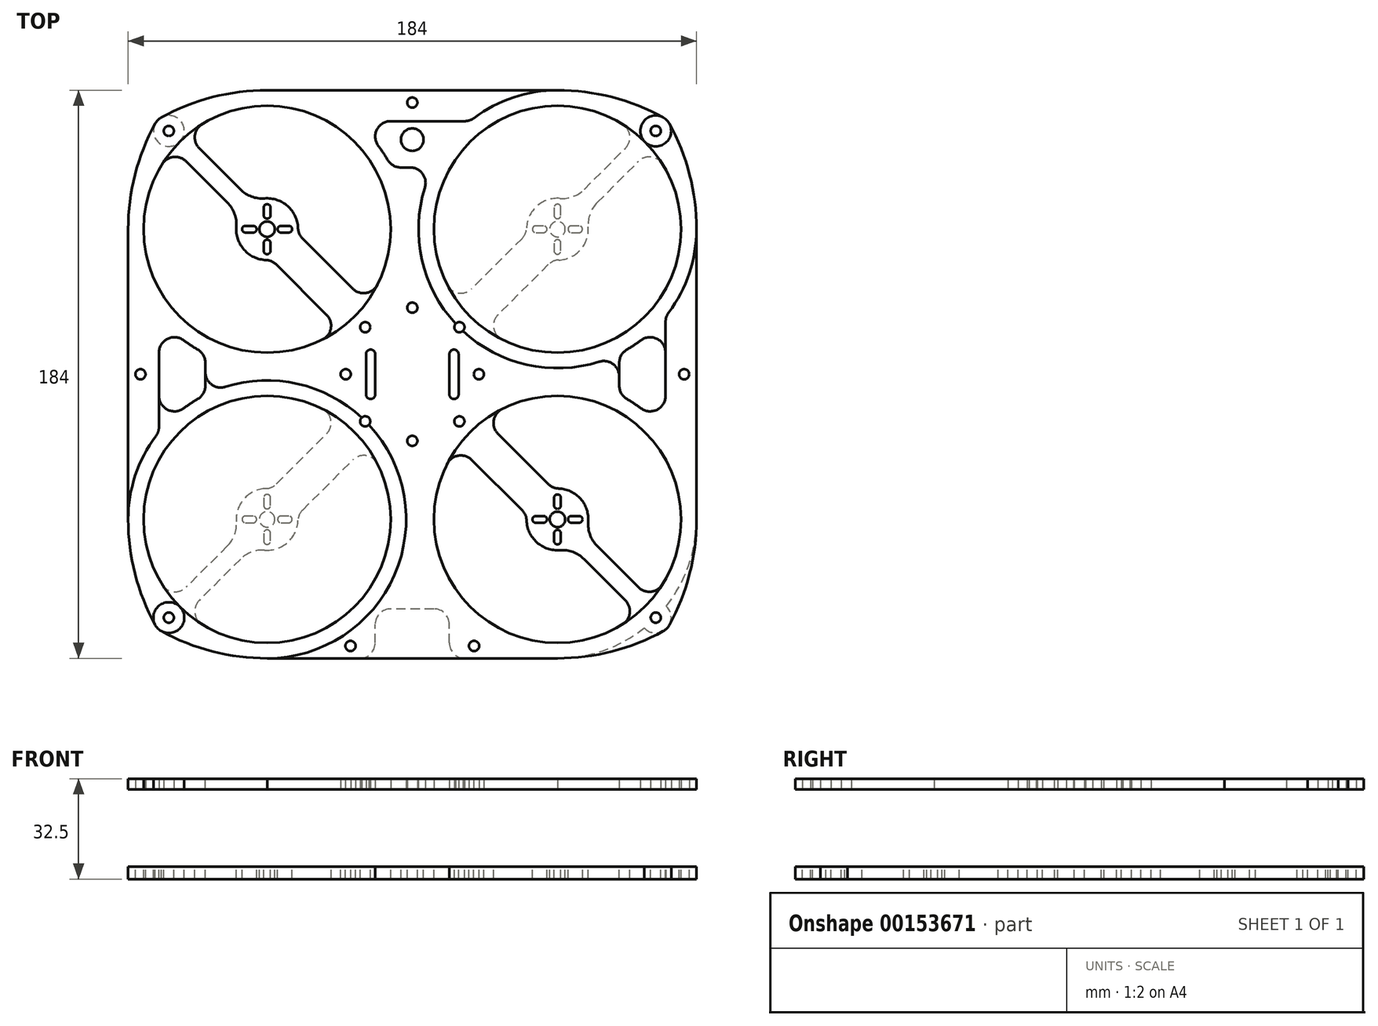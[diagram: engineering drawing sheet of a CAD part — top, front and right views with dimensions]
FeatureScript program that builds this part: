
annotation { "Feature Type Name" : "Feature", "Feature Type Description" : "" }
export const myFeature = defineFeature(function(context is Context, id is Id, definition is map)
    precondition{}
    {
        {
            var Q0;
            Q0=qCreatedBy(makeId("Top.planeOp"),FACE);
            var sketch = newSketch(context, id + "F0", { "sketchPlane" : qUnion([Q0])});
            skCircle(sketch, "E0", {"center": v(-83.32, 39.77) * mm, "radius": 40 * mm});
            skCircle(sketch, "E1", {"center": v(-83.32, 39.77) * mm, "radius": 45 * mm});
            skLineSegment(sketch, "E2", {"start": v(-154.39, -7.23) * mm, "end": v(73.7, -7.23) * mm, "construction": true});
            skLineSegment(sketch, "E3", {"start": v(-36.32, 93.26) * mm, "end": v(-36.32, -114.87) * mm, "construction": true});
            skCircle(sketch, "E4.MirrorC", {"center": v(10.68, 39.77) * mm, "radius": 45 * mm});
            skCircle(sketch, "E5.MirrorC", {"center": v(10.68, 39.77) * mm, "radius": 40 * mm});
            skCircle(sketch, "E6.MirrorC", {"center": v(-83.32, -54.23) * mm, "radius": 40 * mm});
            skCircle(sketch, "E7.MirrorC", {"center": v(-83.32, -54.23) * mm, "radius": 45 * mm});
            skCircle(sketch, "E8.MirrorC", {"center": v(10.68, -54.23) * mm, "radius": 45 * mm});
            skCircle(sketch, "E9.MirrorC", {"center": v(10.68, -54.23) * mm, "radius": 40 * mm});
            skCircle(sketch, "E10", {"center": v(-57.88, -7.23) * mm, "radius": 1.65 * mm});
            skCircle(sketch, "E11", {"center": v(-36.32, 14.33) * mm, "radius": 1.65 * mm});
            skCircle(sketch, "E12", {"center": v(-36.32, -28.8) * mm, "radius": 1.65 * mm});
            skCircle(sketch, "E13", {"center": v(-14.75, -7.23) * mm, "radius": 1.65 * mm});
            skLineSegment(sketch, "E14", {"start": v(-36.32, 14.33) * mm, "end": v(-14.75, -7.23) * mm, "construction": true});
            skLineSegment(sketch, "E15", {"start": v(-57.88, -7.23) * mm, "end": v(-36.32, -28.8) * mm, "construction": true});
            skLineSegment(sketch, "E16", {"start": v(-57.88, -7.23) * mm, "end": v(-36.32, 14.33) * mm, "construction": true});
            skLineSegment(sketch, "E17", {"start": v(-36.32, -28.8) * mm, "end": v(-14.75, -7.23) * mm, "construction": true});
            skLineSegment(sketch, "E18", {"start": v(-36.32, 21.33) * mm, "end": v(-7.75, -7.23) * mm, "construction": true});
            skLineSegment(sketch, "E19", {"start": v(-7.75, -7.23) * mm, "end": v(-36.32, -35.8) * mm, "construction": true});
            skLineSegment(sketch, "E20", {"start": v(-36.32, -35.8) * mm, "end": v(-64.88, -7.23) * mm, "construction": true});
            skLineSegment(sketch, "E21", {"start": v(-64.88, -7.23) * mm, "end": v(-36.32, 21.33) * mm, "construction": true});
            skLineSegment(sketch, "E22", {"start": v(-83.32, 84.77) * mm, "end": v(10.68, 84.77) * mm});
            skLineSegment(sketch, "E23", {"start": v(55.68, 39.77) * mm, "end": v(55.68, -54.23) * mm});
            skLineSegment(sketch, "E24", {"start": v(-83.32, -99.23) * mm, "end": v(10.68, -99.23) * mm});
            skLineSegment(sketch, "E25", {"start": v(-128.32, -54.23) * mm, "end": v(-128.32, 39.77) * mm});
            skLineSegment(sketch, "E26", {"start": v(45.68, -25.95) * mm, "end": v(45.68, 11.48) * mm});
            skLineSegment(sketch, "E27", {"start": v(-118.32, 11.48) * mm, "end": v(-118.32, -25.95) * mm});
            skLineSegment(sketch, "E28", {"start": v(30.68, -0.55) * mm, "end": v(30.68, -13.92) * mm});
            skLineSegment(sketch, "E29", {"start": v(-103.32, -0.55) * mm, "end": v(-103.32, -13.92) * mm});
            skLineSegment(sketch, "E30", {"start": v(-55.03, 74.77) * mm, "end": v(-17.6, 74.77) * mm});
            skLineSegment(sketch, "E31", {"start": v(-43, 59.77) * mm, "end": v(-29.63, 59.77) * mm});
            skCircle(sketch, "E32", {"center": v(-51.57, -22.48) * mm, "radius": 1.65 * mm});
            skCircle(sketch, "E33.MirrorC", {"center": v(-21.07, -22.48) * mm, "radius": 1.65 * mm});
            skCircle(sketch, "E34.MirrorC", {"center": v(-21.07, 8.02) * mm, "radius": 1.65 * mm});
            skCircle(sketch, "E35.MirrorC", {"center": v(-51.57, 8.02) * mm, "radius": 1.65 * mm});
            skCircle(sketch, "E36", {"center": v(-124.32, -7.23) * mm, "radius": 1.65 * mm});
            skCircle(sketch, "E37.MirrorC", {"center": v(51.68, -7.23) * mm, "radius": 1.65 * mm});
            skCircle(sketch, "E38", {"center": v(-36.32, 80.77) * mm, "radius": 1.65 * mm});
            skCircle(sketch, "E39", {"center": v(-56.32, -95.23) * mm, "radius": 1.65 * mm});
            skCircle(sketch, "E40.MirrorC", {"center": v(-16.32, -95.23) * mm, "radius": 1.65 * mm});
            skLineSegment(sketch, "E41.bottom", {"start": v(-51.32, -15.23) * mm, "end": v(-48.32, -15.23) * mm});
            skLineSegment(sketch, "E41.top", {"start": v(-51.32, 0.77) * mm, "end": v(-48.32, 0.77) * mm});
            skLineSegment(sketch, "E41.left", {"start": v(-51.32, -15.23) * mm, "end": v(-51.32, 0.77) * mm});
            skLineSegment(sketch, "E41.right", {"start": v(-48.32, -15.23) * mm, "end": v(-48.32, 0.77) * mm});
            skLineSegment(sketch, "E42.MirrorCS", {"start": v(-66.32, 93.26) * mm, "end": v(-66.32, -114.87) * mm, "construction": true});
            skLineSegment(sketch, "E43.MirrorCS", {"start": v(-24.32, -15.23) * mm, "end": v(-24.32, 0.77) * mm});
            skLineSegment(sketch, "E44.MirrorCS", {"start": v(-21.32, -15.23) * mm, "end": v(-24.32, -15.23) * mm});
            skLineSegment(sketch, "E45.MirrorCS", {"start": v(-21.32, -15.23) * mm, "end": v(-21.32, 0.77) * mm});
            skLineSegment(sketch, "E46.MirrorCS", {"start": v(-21.32, 0.77) * mm, "end": v(-24.32, 0.77) * mm});
            skLineSegment(sketch, "E47", {"start": v(-36.32, -7.23) * mm, "end": v(65.94, 95.02) * mm, "construction": true});
            skLineSegment(sketch, "E48", {"start": v(-36.32, -7.23) * mm, "end": v(-157.97, 114.42) * mm, "construction": true});
            skCircle(sketch, "E49", {"center": v(-115.14, 71.59) * mm, "radius": 1.65 * mm});
            skCircle(sketch, "E50", {"center": v(-115.14, 71.59) * mm, "radius": 5 * mm});
            skArc(sketch, "E51", {"start": v(-83.32, 84.77) * mm, "mid": v(-100.99, 82.53) * mm, "end": v(-117.55, 75.97) * mm});
            skArc(sketch, "E52", {"start": v(-119.52, 74) * mm, "mid": v(-126.08, 57.44) * mm, "end": v(-128.32, 39.77) * mm});
            skArc(sketch, "E53.MirrorCS", {"start": v(10.68, 84.77) * mm, "mid": v(28.36, 82.53) * mm, "end": v(44.92, 75.97) * mm});
            skArc(sketch, "E54.MirrorCS", {"start": v(46.88, 74) * mm, "mid": v(53.45, 57.44) * mm, "end": v(55.68, 39.77) * mm});
            skCircle(sketch, "E55.MirrorC", {"center": v(42.5, 71.59) * mm, "radius": 1.65 * mm});
            skCircle(sketch, "E56.MirrorC", {"center": v(42.5, 71.59) * mm, "radius": 5 * mm});
            skArc(sketch, "E57.MirrorCS", {"start": v(46.88, -88.47) * mm, "mid": v(53.45, -71.9) * mm, "end": v(55.68, -54.23) * mm});
            skCircle(sketch, "E58.MirrorC", {"center": v(42.5, -86.05) * mm, "radius": 5 * mm});
            skCircle(sketch, "E59.MirrorC", {"center": v(42.5, -86.05) * mm, "radius": 1.65 * mm});
            skArc(sketch, "E60.MirrorCS", {"start": v(10.68, -99.23) * mm, "mid": v(28.36, -97) * mm, "end": v(44.92, -90.43) * mm});
            skArc(sketch, "E61.MirrorCS", {"start": v(-83.32, -99.23) * mm, "mid": v(-100.99, -97) * mm, "end": v(-117.55, -90.43) * mm});
            skCircle(sketch, "E62.MirrorC", {"center": v(-115.14, -86.05) * mm, "radius": 5 * mm});
            skCircle(sketch, "E63.MirrorC", {"center": v(-115.14, -86.05) * mm, "radius": 1.65 * mm});
            skArc(sketch, "E64.MirrorCS", {"start": v(-119.52, -88.47) * mm, "mid": v(-126.08, -71.9) * mm, "end": v(-128.32, -54.23) * mm});
            skSolve(sketch);
        }
        {
            var Q0;
            {var subQ0=sQuery(id+"F0.wireOp",EDGE,"E25");Q0=makeQuery(id+"F0.imprint","IMPRINT",FACE,{"disambiguationData":[TD([[makeQuery(id+"F0.imprint","IMPRINT",EDGE,{"derivedFrom":subQ0}),-1.0]])]});}
            var Q1;
            Q1=makeQuery(id+"F0.imprint","IMPRINT",FACE,{"disambiguationData":[TD([[makeQuery(id+"F0.imprint","IMPRINT",EDGE,{"derivedFrom":sQuery(id+"F0.wireOp",EDGE,"E0")}),-1.0]])]});
            var Q2;
            Q2=makeQuery(id+"F0.imprint","IMPRINT",FACE,{"disambiguationData":[TD([[makeQuery(id+"F0.imprint","IMPRINT",EDGE,{"derivedFrom":sQuery(id+"F0.wireOp",EDGE,"E10")}),-1.0]])]});
            var Q3;
            Q3=makeQuery(id+"F0.imprint","IMPRINT",FACE,{"disambiguationData":[TD([[makeQuery(id+"F0.imprint","IMPRINT",EDGE,{"derivedFrom":sQuery(id+"F0.wireOp",EDGE,"E5.MirrorC")}),1.0]])]});
            var Q4;
            {var subQ0=sQuery(id+"F0.wireOp",EDGE,"E23");Q4=makeQuery(id+"F0.imprint","IMPRINT",FACE,{"disambiguationData":[TD([[makeQuery(id+"F0.imprint","IMPRINT",EDGE,{"derivedFrom":subQ0}),-1.0]])]});}
            var Q5;
            Q5=makeQuery(id+"F0.imprint","IMPRINT",FACE,{"disambiguationData":[TD([[makeQuery(id+"F0.imprint","IMPRINT",EDGE,{"derivedFrom":sQuery(id+"F0.wireOp",EDGE,"E6.MirrorC")}),1.0]])]});
            var Q6;
            Q6=makeQuery(id+"F0.imprint","IMPRINT",FACE,{"disambiguationData":[TD([[makeQuery(id+"F0.imprint","IMPRINT",EDGE,{"derivedFrom":sQuery(id+"F0.wireOp",EDGE,"E9.MirrorC")}),-1.0]])]});
            var Q7;
            {var subQ0=sQuery(id+"F0.wireOp",EDGE,"E22");Q7=makeQuery(id+"F0.imprint","IMPRINT",FACE,{"disambiguationData":[TD([[makeQuery(id+"F0.imprint","IMPRINT",EDGE,{"derivedFrom":subQ0}),-1.0]])]});}
            var Q8;
            {var subQ0=sQuery(id+"F0.wireOp",EDGE,"E50");var subQ2=sQuery(id+"F0.wireOp",EDGE,"E1");var subQ4=makeQuery(id+"F0.imprint","INTERSECT",VERTEX,{"disambiguationData":[OD(0.0)],"derivedFrom":[subQ2,subQ0]});Q8=makeQuery(id+"F0.imprint","IMPRINT",FACE,{"disambiguationData":[TD([[makeQuery(id+"F0.imprint","IMPRINT",EDGE,{"disambiguationData":[TD([[subQ4,-1.0]])],"derivedFrom":subQ2}),1.0]])]});}
            var Q9;
            {var subQ0=sQuery(id+"F0.wireOp",EDGE,"E51");Q9=makeQuery(id+"F0.imprint","IMPRINT",FACE,{"disambiguationData":[TD([[makeQuery(id+"F0.imprint","IMPRINT",EDGE,{"derivedFrom":subQ0}),1.0]])]});}
            var Q10;
            {var subQ0=sQuery(id+"F0.wireOp",EDGE,"E50");var subQ2=sQuery(id+"F0.wireOp",EDGE,"E1");var subQ3=makeQuery(id+"F0.imprint","INTERSECT",VERTEX,{"disambiguationData":[OD(0.0)],"derivedFrom":[subQ2,subQ0]});Q10=makeQuery(id+"F0.imprint","IMPRINT",FACE,{"disambiguationData":[TD([[makeQuery(id+"F0.imprint","IMPRINT",EDGE,{"disambiguationData":[TD([[subQ3,-1.0]])],"derivedFrom":subQ2}),-1.0]])]});}
            var Q11;
            {var subQ0=sQuery(id+"F0.wireOp",EDGE,"E52");Q11=makeQuery(id+"F0.imprint","IMPRINT",FACE,{"disambiguationData":[TD([[makeQuery(id+"F0.imprint","IMPRINT",EDGE,{"derivedFrom":subQ0}),1.0]])]});}
            var Q12;
            {var subQ0=sQuery(id+"F0.wireOp",EDGE,"E54.MirrorCS");Q12=makeQuery(id+"F0.imprint","IMPRINT",FACE,{"disambiguationData":[TD([[makeQuery(id+"F0.imprint","IMPRINT",EDGE,{"derivedFrom":subQ0}),-1.0]])]});}
            var Q13;
            {var subQ1=sQuery(id+"F0.wireOp",EDGE,"E4.MirrorC");var subQ4=sQuery(id+"F0.wireOp",EDGE,"E56.MirrorC");var subQ6=makeQuery(id+"F0.imprint","INTERSECT",VERTEX,{"disambiguationData":[OD(0.0)],"derivedFrom":[subQ1,subQ4]});Q13=makeQuery(id+"F0.imprint","IMPRINT",FACE,{"disambiguationData":[TD([[makeQuery(id+"F0.imprint","IMPRINT",EDGE,{"disambiguationData":[TD([[subQ6,-1.0]])],"derivedFrom":subQ1}),1.0]])]});}
            var Q14;
            {var subQ0=sQuery(id+"F0.wireOp",EDGE,"E53.MirrorCS");Q14=makeQuery(id+"F0.imprint","IMPRINT",FACE,{"disambiguationData":[TD([[makeQuery(id+"F0.imprint","IMPRINT",EDGE,{"derivedFrom":subQ0}),-1.0]])]});}
            var Q15;
            {var subQ1=sQuery(id+"F0.wireOp",EDGE,"E4.MirrorC");var subQ4=sQuery(id+"F0.wireOp",EDGE,"E56.MirrorC");var subQ7=makeQuery(id+"F0.imprint","INTERSECT",VERTEX,{"disambiguationData":[OD(0.0)],"derivedFrom":[subQ1,subQ4]});Q15=makeQuery(id+"F0.imprint","IMPRINT",FACE,{"disambiguationData":[TD([[makeQuery(id+"F0.imprint","IMPRINT",EDGE,{"disambiguationData":[TD([[subQ7,-1.0]])],"derivedFrom":subQ1}),-1.0]])]});}
            var Q16;
            {var subQ0=sQuery(id+"F0.wireOp",EDGE,"E28");Q16=makeQuery(id+"F0.imprint","IMPRINT",FACE,{"disambiguationData":[TD([[makeQuery(id+"F0.imprint","IMPRINT",EDGE,{"derivedFrom":subQ0}),-1.0]])]});}
            var Q17;
            {var subQ0=sQuery(id+"F0.wireOp",EDGE,"E29");Q17=makeQuery(id+"F0.imprint","IMPRINT",FACE,{"disambiguationData":[TD([[makeQuery(id+"F0.imprint","IMPRINT",EDGE,{"derivedFrom":subQ0}),1.0]])]});}
            var Q18;
            {var subQ0=sQuery(id+"F0.wireOp",EDGE,"E58.MirrorC");var subQ4=sQuery(id+"F0.wireOp",EDGE,"E8.MirrorC");var subQ7=makeQuery(id+"F0.imprint","INTERSECT",VERTEX,{"disambiguationData":[OD(0.0)],"derivedFrom":[subQ4,subQ0]});Q18=makeQuery(id+"F0.imprint","IMPRINT",FACE,{"disambiguationData":[TD([[makeQuery(id+"F0.imprint","IMPRINT",EDGE,{"disambiguationData":[TD([[subQ7,-1.0]])],"derivedFrom":subQ4}),-1.0]])]});}
            var Q19;
            {var subQ0=sQuery(id+"F0.wireOp",EDGE,"E57.MirrorCS");Q19=makeQuery(id+"F0.imprint","IMPRINT",FACE,{"disambiguationData":[TD([[makeQuery(id+"F0.imprint","IMPRINT",EDGE,{"derivedFrom":subQ0}),1.0]])]});}
            var Q20;
            {var subQ0=sQuery(id+"F0.wireOp",EDGE,"E58.MirrorC");var subQ2=sQuery(id+"F0.wireOp",EDGE,"E8.MirrorC");var subQ3=makeQuery(id+"F0.imprint","INTERSECT",VERTEX,{"disambiguationData":[OD(0.0)],"derivedFrom":[subQ2,subQ0]});Q20=makeQuery(id+"F0.imprint","IMPRINT",FACE,{"disambiguationData":[TD([[makeQuery(id+"F0.imprint","IMPRINT",EDGE,{"disambiguationData":[TD([[subQ3,-1.0]])],"derivedFrom":subQ2}),1.0]])]});}
            var Q21;
            {var subQ0=sQuery(id+"F0.wireOp",EDGE,"E60.MirrorCS");Q21=makeQuery(id+"F0.imprint","IMPRINT",FACE,{"disambiguationData":[TD([[makeQuery(id+"F0.imprint","IMPRINT",EDGE,{"derivedFrom":subQ0}),1.0]])]});}
            var Q22;
            {var subQ0=sQuery(id+"F0.wireOp",EDGE,"E61.MirrorCS");Q22=makeQuery(id+"F0.imprint","IMPRINT",FACE,{"disambiguationData":[TD([[makeQuery(id+"F0.imprint","IMPRINT",EDGE,{"derivedFrom":subQ0}),-1.0]])]});}
            var Q23;
            {var subQ0=sQuery(id+"F0.wireOp",EDGE,"E62.MirrorC");var subQ2=sQuery(id+"F0.wireOp",EDGE,"E7.MirrorC");var subQ3=makeQuery(id+"F0.imprint","INTERSECT",VERTEX,{"disambiguationData":[OD(0.0)],"derivedFrom":[subQ2,subQ0]});Q23=makeQuery(id+"F0.imprint","IMPRINT",FACE,{"disambiguationData":[TD([[makeQuery(id+"F0.imprint","IMPRINT",EDGE,{"disambiguationData":[TD([[subQ3,-1.0]])],"derivedFrom":subQ2}),1.0]])]});}
            var Q24;
            {var subQ1=sQuery(id+"F0.wireOp",EDGE,"E7.MirrorC");var subQ3=sQuery(id+"F0.wireOp",EDGE,"E62.MirrorC");var subQ6=makeQuery(id+"F0.imprint","INTERSECT",VERTEX,{"disambiguationData":[OD(0.0)],"derivedFrom":[subQ1,subQ3]});Q24=makeQuery(id+"F0.imprint","IMPRINT",FACE,{"disambiguationData":[TD([[makeQuery(id+"F0.imprint","IMPRINT",EDGE,{"disambiguationData":[TD([[subQ6,-1.0]])],"derivedFrom":subQ1}),-1.0]])]});}
            var Q25;
            {var subQ0=sQuery(id+"F0.wireOp",EDGE,"E64.MirrorCS");Q25=makeQuery(id+"F0.imprint","IMPRINT",FACE,{"disambiguationData":[TD([[makeQuery(id+"F0.imprint","IMPRINT",EDGE,{"derivedFrom":subQ0}),-1.0]])]});}
            extrude(context, id + "F1", {"entities" : qUnion([Q0, Q1, Q2, Q3, Q4, Q5, Q6, Q7, Q8, Q9, Q10, Q11, Q12, Q13, Q14, Q15, Q16, Q17, Q18, Q19, Q20, Q21, Q22, Q23, Q24, Q25]), "depth" : 3.5 * mm});
        }
        {
            var Q0;
            Q0=makeQuery(id+"F1.opExtrude","SWEPT_EDGE",EDGE,{"disambiguationData":[OSD([sQuery(id+"F0.wireOp",EDGE,"E1"),sQuery(id+"F0.wireOp",EDGE,"E27")])]});
            var Q1;
            Q1=makeQuery(id+"F1.opExtrude","SWEPT_EDGE",EDGE,{"disambiguationData":[OSD([sQuery(id+"F0.wireOp",EDGE,"E4.MirrorC"),sQuery(id+"F0.wireOp",EDGE,"E26")])]});
            var Q2;
            Q2=makeQuery(id+"F1.opExtrude","SWEPT_EDGE",EDGE,{"disambiguationData":[OSD([sQuery(id+"F0.wireOp",EDGE,"E8.MirrorC"),sQuery(id+"F0.wireOp",EDGE,"E26")])]});
            var Q3;
            Q3=makeQuery(id+"F1.opExtrude","SWEPT_EDGE",EDGE,{"disambiguationData":[OSD([sQuery(id+"F0.wireOp",EDGE,"E7.MirrorC"),sQuery(id+"F0.wireOp",EDGE,"E27")])]});
            var Q4;
            Q4=makeQuery(id+"F1.opExtrude","SWEPT_EDGE",EDGE,{"disambiguationData":[OSD([sQuery(id+"F0.wireOp",EDGE,"E4.MirrorC"),sQuery(id+"F0.wireOp",EDGE,"E30")])]});
            var Q5;
            Q5=makeQuery(id+"F1.opExtrude","SWEPT_EDGE",EDGE,{"disambiguationData":[OSD([sQuery(id+"F0.wireOp",EDGE,"E1"),sQuery(id+"F0.wireOp",EDGE,"E30")])]});
            fillet(context, id + "F2", {"entities" : qUnion([Q0, Q1, Q2, Q3, Q4, Q5]), "radius" : 5 * mm, "tangentPropagation" : true, "allowEdgeOverflow" : false});
        }
        {
            var Q0;
            Q0=makeQuery(id+"F1.opExtrude","SWEPT_EDGE",EDGE,{"disambiguationData":[OSD([sQuery(id+"F0.wireOp",EDGE,"E4.MirrorC"),sQuery(id+"F0.wireOp",EDGE,"E28")])]});
            var Q1;
            Q1=makeQuery(id+"F1.opExtrude","SWEPT_EDGE",EDGE,{"disambiguationData":[OSD([sQuery(id+"F0.wireOp",EDGE,"E8.MirrorC"),sQuery(id+"F0.wireOp",EDGE,"E28")])]});
            var Q2;
            Q2=makeQuery(id+"F1.opExtrude","SWEPT_EDGE",EDGE,{"disambiguationData":[OSD([sQuery(id+"F0.wireOp",EDGE,"E1"),sQuery(id+"F0.wireOp",EDGE,"E29")])]});
            var Q3;
            Q3=makeQuery(id+"F1.opExtrude","SWEPT_EDGE",EDGE,{"disambiguationData":[OSD([sQuery(id+"F0.wireOp",EDGE,"E7.MirrorC"),sQuery(id+"F0.wireOp",EDGE,"E29")])]});
            var Q4;
            Q4=makeQuery(id+"F1.opExtrude","SWEPT_EDGE",EDGE,{"disambiguationData":[OSD([sQuery(id+"F0.wireOp",EDGE,"E4.MirrorC"),sQuery(id+"F0.wireOp",EDGE,"E31")])]});
            var Q5;
            Q5=makeQuery(id+"F1.opExtrude","SWEPT_EDGE",EDGE,{"disambiguationData":[OSD([sQuery(id+"F0.wireOp",EDGE,"E1"),sQuery(id+"F0.wireOp",EDGE,"E31")])]});
            fillet(context, id + "F3", {"entities" : qUnion([Q0, Q1, Q2, Q3, Q4, Q5]), "radius" : 5 * mm, "tangentPropagation" : true, "allowEdgeOverflow" : false});
        }
        {
            var Q0;
            Q0=makeQuery(id+"F1.opExtrude","SWEPT_EDGE",EDGE,{"disambiguationData":[OSD([sQuery(id+"F0.wireOp",EDGE,"E41.bottom"),sQuery(id+"F0.wireOp",EDGE,"E41.left")])]});
            var Q1;
            Q1=makeQuery(id+"F1.opExtrude","SWEPT_EDGE",EDGE,{"disambiguationData":[OSD([sQuery(id+"F0.wireOp",EDGE,"E43.MirrorCS"),sQuery(id+"F0.wireOp",EDGE,"E44.MirrorCS")])]});
            var Q2;
            Q2=makeQuery(id+"F1.opExtrude","SWEPT_EDGE",EDGE,{"disambiguationData":[OSD([sQuery(id+"F0.wireOp",EDGE,"E41.bottom"),sQuery(id+"F0.wireOp",EDGE,"E41.right")])]});
            var Q3;
            Q3=makeQuery(id+"F1.opExtrude","SWEPT_EDGE",EDGE,{"disambiguationData":[OSD([sQuery(id+"F0.wireOp",EDGE,"E44.MirrorCS"),sQuery(id+"F0.wireOp",EDGE,"E45.MirrorCS")])]});
            var Q4;
            Q4=makeQuery(id+"F1.opExtrude","SWEPT_EDGE",EDGE,{"disambiguationData":[OSD([sQuery(id+"F0.wireOp",EDGE,"E43.MirrorCS"),sQuery(id+"F0.wireOp",EDGE,"E46.MirrorCS")])]});
            var Q5;
            Q5=makeQuery(id+"F1.opExtrude","SWEPT_EDGE",EDGE,{"disambiguationData":[OSD([sQuery(id+"F0.wireOp",EDGE,"E41.top"),sQuery(id+"F0.wireOp",EDGE,"E41.left")])]});
            var Q6;
            Q6=makeQuery(id+"F1.opExtrude","SWEPT_EDGE",EDGE,{"disambiguationData":[OSD([sQuery(id+"F0.wireOp",EDGE,"E45.MirrorCS"),sQuery(id+"F0.wireOp",EDGE,"E46.MirrorCS")])]});
            var Q7;
            Q7=makeQuery(id+"F1.opExtrude","SWEPT_EDGE",EDGE,{"disambiguationData":[OSD([sQuery(id+"F0.wireOp",EDGE,"E41.top"),sQuery(id+"F0.wireOp",EDGE,"E41.right")])]});
            fillet(context, id + "F4", {"entities" : qUnion([Q0, Q1, Q2, Q3, Q4, Q5, Q6, Q7]), "radius" : 1.5 * mm, "tangentPropagation" : true, "allowEdgeOverflow" : false});
        }
        {
            var Q0;
            Q0=makeQuery(id+"F1.opExtrude","CAP_FACE",FACE,{"disambiguationData":[OSD([sQuery(id+"F0.wireOp",EDGE,"E0"),sQuery(id+"F0.wireOp",EDGE,"E1"),sQuery(id+"F0.wireOp",EDGE,"E4.MirrorC"),sQuery(id+"F0.wireOp",EDGE,"E5.MirrorC"),sQuery(id+"F0.wireOp",EDGE,"E6.MirrorC"),sQuery(id+"F0.wireOp",EDGE,"E7.MirrorC"),sQuery(id+"F0.wireOp",EDGE,"E8.MirrorC"),sQuery(id+"F0.wireOp",EDGE,"E9.MirrorC"),sQuery(id+"F0.wireOp",EDGE,"E10"),sQuery(id+"F0.wireOp",EDGE,"E11"),sQuery(id+"F0.wireOp",EDGE,"E12"),sQuery(id+"F0.wireOp",EDGE,"E13"),sQuery(id+"F0.wireOp",EDGE,"E22"),sQuery(id+"F0.wireOp",EDGE,"E23"),sQuery(id+"F0.wireOp",EDGE,"E24"),sQuery(id+"F0.wireOp",EDGE,"E25"),sQuery(id+"F0.wireOp",EDGE,"E26"),sQuery(id+"F0.wireOp",EDGE,"E27"),sQuery(id+"F0.wireOp",EDGE,"E28"),sQuery(id+"F0.wireOp",EDGE,"E29"),sQuery(id+"F0.wireOp",EDGE,"E30"),sQuery(id+"F0.wireOp",EDGE,"E31"),sQuery(id+"F0.wireOp",EDGE,"E32"),sQuery(id+"F0.wireOp",EDGE,"E33.MirrorC"),sQuery(id+"F0.wireOp",EDGE,"E34.MirrorC"),sQuery(id+"F0.wireOp",EDGE,"E35.MirrorC"),sQuery(id+"F0.wireOp",EDGE,"E36"),sQuery(id+"F0.wireOp",EDGE,"E37.MirrorC"),sQuery(id+"F0.wireOp",EDGE,"E38"),sQuery(id+"F0.wireOp",EDGE,"E39"),sQuery(id+"F0.wireOp",EDGE,"E40.MirrorC"),sQuery(id+"F0.wireOp",EDGE,"E41.bottom"),sQuery(id+"F0.wireOp",EDGE,"E41.top"),sQuery(id+"F0.wireOp",EDGE,"E41.left"),sQuery(id+"F0.wireOp",EDGE,"E41.right"),sQuery(id+"F0.wireOp",EDGE,"E43.MirrorCS"),sQuery(id+"F0.wireOp",EDGE,"E44.MirrorCS"),sQuery(id+"F0.wireOp",EDGE,"E45.MirrorCS"),sQuery(id+"F0.wireOp",EDGE,"E46.MirrorCS")])],"isStart":true});
            cPlane(context, id + "F5", {"entities" : qUnion([Q0]), "cplaneType" : CPlaneType.OFFSET, "offset" : 25 * mm, "width" : 150 * mm, "height" : 150 * mm});
        }
        {
            var Q0;
            Q0=qCreatedBy(id+"F5.planeOp",FACE);
            var sketch = newSketch(context, id + "F6", { "sketchPlane" : qUnion([Q0])});
            skLineSegment(sketch, "E65.0", {"start": v(-110.32, 18.23) * mm, "end": v(-110.32, 18.23) * mm});
            skLineSegment(sketch, "E66.0", {"start": v(-128.32, 57.23) * mm, "end": v(-128.32, -39.77) * mm});
            skLineSegment(sketch, "E67.0", {"start": v(-83.32, -84.77) * mm, "end": v(10.68, -84.77) * mm});
            skLineSegment(sketch, "E68.0", {"start": v(55.68, -39.77) * mm, "end": v(55.68, 54.23) * mm});
            skLineSegment(sketch, "E69.0", {"start": v(-86.32, 99.23) * mm, "end": v(10.68, 99.23) * mm});
            skArc(sketch, "E70.0", {"start": v(10.68, 99.23) * mm, "mid": v(42.5, 86.05) * mm, "end": v(55.68, 54.23) * mm});
            skCircle(sketch, "E71.0", {"center": v(51.68, 7.23) * mm, "radius": 1.65 * mm});
            skCircle(sketch, "E72.0", {"center": v(-16.32, 95.23) * mm, "radius": 1.65 * mm});
            skCircle(sketch, "E73.0", {"center": v(-56.32, 95.23) * mm, "radius": 1.65 * mm});
            skCircle(sketch, "E74.0", {"center": v(-124.32, 7.23) * mm, "radius": 1.65 * mm});
            skCircle(sketch, "E75.0", {"center": v(-36.32, -80.77) * mm, "radius": 1.65 * mm});
            skCircle(sketch, "E76.0", {"center": v(10.68, -39.77) * mm, "radius": 40 * mm});
            skCircle(sketch, "E77.0", {"center": v(-83.32, -39.77) * mm, "radius": 40 * mm});
            skCircle(sketch, "E78.0", {"center": v(-83.32, 54.23) * mm, "radius": 40 * mm});
            skCircle(sketch, "E79.0", {"center": v(10.68, 54.23) * mm, "radius": 40 * mm});
            skLineSegment(sketch, "E80.0", {"start": v(-21.32, 13.73) * mm, "end": v(-21.32, 0.73) * mm});
            skLineSegment(sketch, "E81.0", {"start": v(-24.32, 13.73) * mm, "end": v(-24.32, 0.73) * mm});
            skLineSegment(sketch, "E82.0", {"start": v(-48.32, 13.73) * mm, "end": v(-48.32, 0.73) * mm});
            skLineSegment(sketch, "E83.0", {"start": v(-51.32, 13.73) * mm, "end": v(-51.32, 0.73) * mm});
            skCircle(sketch, "E84.0", {"center": v(-51.57, 22.48) * mm, "radius": 1.65 * mm});
            skCircle(sketch, "E85.0", {"center": v(-36.32, 28.8) * mm, "radius": 1.65 * mm});
            skCircle(sketch, "E86.0", {"center": v(-14.75, 7.23) * mm, "radius": 1.65 * mm});
            skCircle(sketch, "E87.0", {"center": v(-36.32, -14.33) * mm, "radius": 1.65 * mm});
            skCircle(sketch, "E88.0", {"center": v(-51.57, -8.02) * mm, "radius": 1.65 * mm});
            skCircle(sketch, "E89.0", {"center": v(-57.88, 7.23) * mm, "radius": 1.65 * mm});
            skCircle(sketch, "E90.0", {"center": v(-21.07, -8.02) * mm, "radius": 1.65 * mm});
            skCircle(sketch, "E91.0", {"center": v(-21.07, 22.48) * mm, "radius": 1.65 * mm});
            skLineSegment(sketch, "E92.0", {"start": v(45.68, 14.23) * mm, "end": v(45.68, 0.23) * mm});
            skArc(sketch, "E92.1", {"start": v(45.68, 0.23) * mm, "mid": v(42.92, -4.24) * mm, "end": v(37.68, -3.77) * mm});
            skLineSegment(sketch, "E92.2", {"start": v(30.68, 3.54) * mm, "end": v(30.68, 10.93) * mm});
            skArc(sketch, "E92.3", {"start": v(37.68, 18.23) * mm, "mid": v(35.48, 16.68) * mm, "end": v(33.18, 15.26) * mm});
            skArc(sketch, "E92.4", {"start": v(37.68, 18.23) * mm, "mid": v(42.92, 18.7) * mm, "end": v(45.68, 14.23) * mm});
            skPoint(sketch, "E92.5", {"position": v(33.18, 15.26) * mm});
            skArc(sketch, "E93.0", {"start": v(30.68, 10.93) * mm, "mid": v(31.35, 13.43) * mm, "end": v(33.18, 15.26) * mm});
            skArc(sketch, "E94.0", {"start": v(33.18, -0.8) * mm, "mid": v(31.35, 1.04) * mm, "end": v(30.68, 3.54) * mm});
            skArc(sketch, "E94.1", {"start": v(37.68, -3.77) * mm, "mid": v(35.48, -2.21) * mm, "end": v(33.18, -0.8) * mm});
            skArc(sketch, "E95.0", {"start": v(-21.32, 0.73) * mm, "mid": v(-22.82, -0.77) * mm, "end": v(-24.32, 0.73) * mm});
            skArc(sketch, "E96.0", {"start": v(-24.32, 13.73) * mm, "mid": v(-22.82, 15.23) * mm, "end": v(-21.32, 13.73) * mm});
            skArc(sketch, "E97.0", {"start": v(-51.32, 13.73) * mm, "mid": v(-49.82, 15.23) * mm, "end": v(-48.32, 13.73) * mm});
            skArc(sketch, "E98.0", {"start": v(-48.32, 0.73) * mm, "mid": v(-49.82, -0.77) * mm, "end": v(-51.32, 0.73) * mm});
            skArc(sketch, "E99.0", {"start": v(-110.32, -3.77) * mm, "mid": v(-108.11, -2.21) * mm, "end": v(-105.82, -0.8) * mm});
            skArc(sketch, "E99.1", {"start": v(-103.32, 3.54) * mm, "mid": v(-103.99, 1.04) * mm, "end": v(-105.82, -0.8) * mm});
            skLineSegment(sketch, "E99.2", {"start": v(-103.32, 3.54) * mm, "end": v(-103.32, 10.93) * mm});
            skArc(sketch, "E99.3", {"start": v(-105.82, 15.26) * mm, "mid": v(-103.99, 13.43) * mm, "end": v(-103.32, 10.93) * mm});
            skArc(sketch, "E99.4", {"start": v(-110.32, 18.23) * mm, "mid": v(-108.11, 16.68) * mm, "end": v(-105.82, 15.26) * mm});
            skArc(sketch, "E99.5", {"start": v(-118.32, 14.23) * mm, "mid": v(-115.55, 18.7) * mm, "end": v(-110.32, 18.23) * mm});
            skLineSegment(sketch, "E99.6", {"start": v(-118.32, 0.23) * mm, "end": v(-118.32, 14.23) * mm});
            skArc(sketch, "E99.7", {"start": v(-110.32, -3.77) * mm, "mid": v(-115.55, -4.24) * mm, "end": v(-118.32, 0.23) * mm});
            skCircle(sketch, "E100", {"center": v(-83.32, 54.23) * mm, "radius": 10 * mm});
            skLineSegment(sketch, "E101.0", {"start": v(-36.32, -93.26) * mm, "end": v(-36.32, 114.87) * mm, "construction": true});
            skLineSegment(sketch, "E102.0", {"start": v(-154.39, 7.23) * mm, "end": v(73.7, 7.23) * mm, "construction": true});
            skLineSegment(sketch, "E103", {"start": v(-36.32, 7.23) * mm, "end": v(-115.14, 86.05) * mm, "construction": true});
            skLineSegment(sketch, "E104", {"start": v(-92.18, 58.86) * mm, "end": v(-113.64, 80.32) * mm});
            skLineSegment(sketch, "E105", {"start": v(-87.94, 63.1) * mm, "end": v(-109.4, 84.56) * mm});
            skCircle(sketch, "E106", {"center": v(-83.32, 54.23) * mm, "radius": 2.5 * mm});
            skLineSegment(sketch, "E107", {"start": v(-83.32, 64.23) * mm, "end": v(-83.32, 44.23) * mm, "construction": true});
            skLineSegment(sketch, "E108", {"start": v(-73.32, 54.23) * mm, "end": v(-93.32, 54.23) * mm, "construction": true});
            skCircle(sketch, "E109", {"center": v(-87.82, 54.23) * mm, "radius": 1.1 * mm});
            skCircle(sketch, "E110", {"center": v(-90.32, 54.23) * mm, "radius": 1.1 * mm});
            skLineSegment(sketch, "E111", {"start": v(-90.32, 55.33) * mm, "end": v(-87.82, 55.33) * mm});
            skLineSegment(sketch, "E112", {"start": v(-87.82, 53.13) * mm, "end": v(-90.32, 53.13) * mm});
            skLineSegment(sketch, "E113.1.0", {"start": v(-82.22, 61.23) * mm, "end": v(-82.22, 58.73) * mm});
            skCircle(sketch, "E113.1.1", {"center": v(-83.32, 58.73) * mm, "radius": 1.1 * mm});
            skLineSegment(sketch, "E113.1.2", {"start": v(-84.42, 58.73) * mm, "end": v(-84.42, 61.23) * mm});
            skCircle(sketch, "E113.1.3", {"center": v(-83.32, 61.23) * mm, "radius": 1.1 * mm});
            skLineSegment(sketch, "E113.2.0", {"start": v(-76.32, 53.13) * mm, "end": v(-78.82, 53.13) * mm});
            skCircle(sketch, "E113.2.1", {"center": v(-78.82, 54.23) * mm, "radius": 1.1 * mm});
            skLineSegment(sketch, "E113.2.2", {"start": v(-78.82, 55.33) * mm, "end": v(-76.32, 55.33) * mm});
            skCircle(sketch, "E113.2.3", {"center": v(-76.32, 54.23) * mm, "radius": 1.1 * mm});
            skLineSegment(sketch, "E113.3.0", {"start": v(-84.42, 47.23) * mm, "end": v(-84.42, 49.73) * mm});
            skCircle(sketch, "E113.3.1", {"center": v(-83.32, 49.73) * mm, "radius": 1.1 * mm});
            skLineSegment(sketch, "E113.3.2", {"start": v(-82.22, 49.73) * mm, "end": v(-82.22, 47.23) * mm});
            skCircle(sketch, "E113.3.3", {"center": v(-83.32, 47.23) * mm, "radius": 1.1 * mm});
            skLineSegment(sketch, "E113.anchor1", {"start": v(-83.32, 54.23) * mm, "end": v(-90.32, 55.33) * mm, "construction": true});
            skLineSegment(sketch, "E113.anchor2", {"start": v(-83.32, 54.23) * mm, "end": v(-84.42, 47.23) * mm, "construction": true});
            skLineSegment(sketch, "E114.MirrorCS", {"start": v(17.68, 55.33) * mm, "end": v(15.18, 55.33) * mm});
            skLineSegment(sketch, "E115.MirrorCS", {"start": v(11.78, 47.23) * mm, "end": v(11.78, 49.73) * mm});
            skCircle(sketch, "E116.MirrorC", {"center": v(6.18, 54.23) * mm, "radius": 1.1 * mm});
            skLineSegment(sketch, "E117.MirrorCS", {"start": v(15.18, 53.13) * mm, "end": v(17.68, 53.13) * mm});
            skCircle(sketch, "E118.MirrorC", {"center": v(15.18, 54.23) * mm, "radius": 1.1 * mm});
            skLineSegment(sketch, "E119.MirrorCS", {"start": v(6.18, 55.33) * mm, "end": v(3.68, 55.33) * mm});
            skCircle(sketch, "E120.MirrorC", {"center": v(3.68, 54.23) * mm, "radius": 1.1 * mm});
            skLineSegment(sketch, "E121.MirrorCS", {"start": v(11.78, 58.73) * mm, "end": v(11.78, 61.23) * mm});
            skLineSegment(sketch, "E122.MirrorCS", {"start": v(9.58, 49.73) * mm, "end": v(9.58, 47.23) * mm});
            skLineSegment(sketch, "E123.MirrorCS", {"start": v(3.68, 53.13) * mm, "end": v(6.18, 53.13) * mm});
            skLineSegment(sketch, "E124.MirrorCS", {"start": v(9.58, 61.23) * mm, "end": v(9.58, 58.73) * mm});
            skCircle(sketch, "E125.MirrorC", {"center": v(10.68, 58.73) * mm, "radius": 1.1 * mm});
            skCircle(sketch, "E126.MirrorC", {"center": v(10.68, 49.73) * mm, "radius": 1.1 * mm});
            skLineSegment(sketch, "E127.MirrorCS", {"start": v(10.68, 54.23) * mm, "end": v(17.68, 55.33) * mm, "construction": true});
            skCircle(sketch, "E128.MirrorC", {"center": v(10.68, 61.23) * mm, "radius": 1.1 * mm});
            skLineSegment(sketch, "E129.MirrorCS", {"start": v(10.68, 54.23) * mm, "end": v(11.78, 47.23) * mm, "construction": true});
            skLineSegment(sketch, "E130.MirrorCS", {"start": v(0.68, 54.23) * mm, "end": v(20.68, 54.23) * mm, "construction": true});
            skCircle(sketch, "E131.MirrorC", {"center": v(17.68, 54.23) * mm, "radius": 1.1 * mm});
            skCircle(sketch, "E132.MirrorC", {"center": v(10.68, 54.23) * mm, "radius": 2.5 * mm});
            skCircle(sketch, "E133.MirrorC", {"center": v(10.68, 47.23) * mm, "radius": 1.1 * mm});
            skLineSegment(sketch, "E134.MirrorCS", {"start": v(19.55, 58.86) * mm, "end": v(41, 80.32) * mm});
            skLineSegment(sketch, "E135.MirrorCS", {"start": v(15.3, 63.1) * mm, "end": v(36.77, 84.56) * mm});
            skCircle(sketch, "E136.MirrorC", {"center": v(10.68, 54.23) * mm, "radius": 10 * mm});
            skLineSegment(sketch, "E137.MirrorCS", {"start": v(-78.82, -40.87) * mm, "end": v(-76.32, -40.87) * mm});
            skLineSegment(sketch, "E138.MirrorCS", {"start": v(-87.82, -38.67) * mm, "end": v(-90.32, -38.67) * mm});
            skLineSegment(sketch, "E139.MirrorCS", {"start": v(-82.22, -46.77) * mm, "end": v(-82.22, -44.27) * mm});
            skCircle(sketch, "E140.MirrorC", {"center": v(-76.32, -39.77) * mm, "radius": 1.1 * mm});
            skLineSegment(sketch, "E141.MirrorCS", {"start": v(-84.42, -32.77) * mm, "end": v(-84.42, -35.27) * mm});
            skCircle(sketch, "E142.MirrorC", {"center": v(-78.82, -39.77) * mm, "radius": 1.1 * mm});
            skLineSegment(sketch, "E143.MirrorCS", {"start": v(-90.32, -40.87) * mm, "end": v(-87.82, -40.87) * mm});
            skLineSegment(sketch, "E144.MirrorCS", {"start": v(-76.32, -38.67) * mm, "end": v(-78.82, -38.67) * mm});
            skCircle(sketch, "E145.MirrorC", {"center": v(-83.32, -46.77) * mm, "radius": 1.1 * mm});
            skCircle(sketch, "E146.MirrorC", {"center": v(-83.32, -44.27) * mm, "radius": 1.1 * mm});
            skCircle(sketch, "E147.MirrorC", {"center": v(-83.32, -35.27) * mm, "radius": 1.1 * mm});
            skCircle(sketch, "E148.MirrorC", {"center": v(-87.82, -39.77) * mm, "radius": 1.1 * mm});
            skLineSegment(sketch, "E149.MirrorCS", {"start": v(-83.32, -39.77) * mm, "end": v(-90.32, -40.87) * mm, "construction": true});
            skCircle(sketch, "E150.MirrorC", {"center": v(-83.32, -32.77) * mm, "radius": 1.1 * mm});
            skLineSegment(sketch, "E151.MirrorCS", {"start": v(-73.32, -39.77) * mm, "end": v(-93.32, -39.77) * mm, "construction": true});
            skLineSegment(sketch, "E152.MirrorCS", {"start": v(-84.42, -44.27) * mm, "end": v(-84.42, -46.77) * mm});
            skLineSegment(sketch, "E153.MirrorCS", {"start": v(-82.22, -35.27) * mm, "end": v(-82.22, -32.77) * mm});
            skCircle(sketch, "E154.MirrorC", {"center": v(-90.32, -39.77) * mm, "radius": 1.1 * mm});
            skLineSegment(sketch, "E155.MirrorCS", {"start": v(-83.32, -39.77) * mm, "end": v(-84.42, -32.77) * mm, "construction": true});
            skCircle(sketch, "E156.MirrorC", {"center": v(-83.32, -39.77) * mm, "radius": 10 * mm});
            skCircle(sketch, "E157.MirrorC", {"center": v(-83.32, -39.77) * mm, "radius": 2.5 * mm});
            skLineSegment(sketch, "E158.MirrorCS", {"start": v(-83.32, -49.77) * mm, "end": v(-83.32, -29.77) * mm, "construction": true});
            skLineSegment(sketch, "E159.MirrorCS", {"start": v(17.68, -40.87) * mm, "end": v(15.18, -40.87) * mm});
            skCircle(sketch, "E160.MirrorC", {"center": v(17.68, -39.77) * mm, "radius": 1.1 * mm});
            skLineSegment(sketch, "E161.MirrorCS", {"start": v(11.78, -32.77) * mm, "end": v(11.78, -35.27) * mm});
            skLineSegment(sketch, "E162.MirrorCS", {"start": v(3.68, -38.67) * mm, "end": v(6.18, -38.67) * mm});
            skCircle(sketch, "E163.MirrorC", {"center": v(3.68, -39.77) * mm, "radius": 1.1 * mm});
            skLineSegment(sketch, "E164.MirrorCS", {"start": v(6.18, -40.87) * mm, "end": v(3.68, -40.87) * mm});
            skCircle(sketch, "E165.MirrorC", {"center": v(10.68, -44.27) * mm, "radius": 1.1 * mm});
            skLineSegment(sketch, "E166.MirrorCS", {"start": v(9.58, -46.77) * mm, "end": v(9.58, -44.27) * mm});
            skLineSegment(sketch, "E167.MirrorCS", {"start": v(0.68, -39.77) * mm, "end": v(20.68, -39.77) * mm, "construction": true});
            skCircle(sketch, "E168.MirrorC", {"center": v(10.68, -46.77) * mm, "radius": 1.1 * mm});
            skLineSegment(sketch, "E169.MirrorCS", {"start": v(9.58, -35.27) * mm, "end": v(9.58, -32.77) * mm});
            skCircle(sketch, "E170.MirrorC", {"center": v(6.18, -39.77) * mm, "radius": 1.1 * mm});
            skLineSegment(sketch, "E171.MirrorCS", {"start": v(10.68, -39.77) * mm, "end": v(11.78, -32.77) * mm, "construction": true});
            skLineSegment(sketch, "E172.MirrorCS", {"start": v(11.78, -44.27) * mm, "end": v(11.78, -46.77) * mm});
            skCircle(sketch, "E173.MirrorC", {"center": v(10.68, -35.27) * mm, "radius": 1.1 * mm});
            skLineSegment(sketch, "E174.MirrorCS", {"start": v(10.68, -39.77) * mm, "end": v(17.68, -40.87) * mm, "construction": true});
            skCircle(sketch, "E175.MirrorC", {"center": v(10.68, -32.77) * mm, "radius": 1.1 * mm});
            skLineSegment(sketch, "E176.MirrorCS", {"start": v(15.18, -38.67) * mm, "end": v(17.68, -38.67) * mm});
            skCircle(sketch, "E177.MirrorC", {"center": v(15.18, -39.77) * mm, "radius": 1.1 * mm});
            skCircle(sketch, "E178.MirrorC", {"center": v(10.68, -39.77) * mm, "radius": 10 * mm});
            skCircle(sketch, "E179.MirrorC", {"center": v(10.68, -39.77) * mm, "radius": 2.5 * mm});
            skLineSegment(sketch, "E180.MirrorCS", {"start": v(19.55, -44.39) * mm, "end": v(41, -65.85) * mm});
            skLineSegment(sketch, "E181.MirrorCS", {"start": v(15.3, -48.63) * mm, "end": v(36.77, -70.1) * mm});
            skLineSegment(sketch, "E182.MirrorCS", {"start": v(-92.18, -44.39) * mm, "end": v(-113.64, -65.85) * mm});
            skLineSegment(sketch, "E183.MirrorCS", {"start": v(-87.94, -48.63) * mm, "end": v(-109.4, -70.1) * mm});
            skCircle(sketch, "E184", {"center": v(-36.32, -68.77) * mm, "radius": 3.65 * mm});
            skLineSegment(sketch, "E185", {"start": v(-48.32, 99.23) * mm, "end": v(-48.32, 83.23) * mm});
            skLineSegment(sketch, "E186", {"start": v(-48.32, 83.23) * mm, "end": v(-36.32, 83.23) * mm});
            skLineSegment(sketch, "E187.MirrorCS", {"start": v(-24.32, 83.23) * mm, "end": v(-36.32, 83.23) * mm});
            skLineSegment(sketch, "E188.MirrorCS", {"start": v(-24.32, 99.23) * mm, "end": v(-24.32, 83.23) * mm});
            skPoint(sketch, "E189.startSnap0", {"position": v(-75.73, 46.64) * mm});
            skLineSegment(sketch, "E190", {"start": v(-81.9, 44.33) * mm, "end": v(-59.6, 22.03) * mm});
            skLineSegment(sketch, "E191", {"start": v(-73.42, 52.82) * mm, "end": v(-51.1, 30.51) * mm});
            skLineSegment(sketch, "E192.MirrorCS", {"start": v(0.78, 52.82) * mm, "end": v(-21.52, 30.51) * mm});
            skLineSegment(sketch, "E193.MirrorCS", {"start": v(9.27, 44.33) * mm, "end": v(-13.04, 22.03) * mm});
            skLineSegment(sketch, "E194.MirrorCS", {"start": v(-81.9, -29.87) * mm, "end": v(-59.6, -7.56) * mm});
            skLineSegment(sketch, "E195.MirrorCS", {"start": v(-73.42, -38.35) * mm, "end": v(-51.1, -16.04) * mm});
            skLineSegment(sketch, "E196.MirrorCS", {"start": v(0.78, -38.35) * mm, "end": v(-21.52, -16.04) * mm});
            skLineSegment(sketch, "E197.MirrorCS", {"start": v(9.27, -29.87) * mm, "end": v(-13.04, -7.56) * mm});
            skArc(sketch, "E198.0", {"start": v(46.88, 88.47) * mm, "mid": v(53.45, 71.9) * mm, "end": v(55.68, 54.23) * mm});
            skArc(sketch, "E199.1", {"start": v(10.68, 99.23) * mm, "mid": v(28.36, 97) * mm, "end": v(44.92, 90.43) * mm});
            skCircle(sketch, "E200.2", {"center": v(42.5, 86.05) * mm, "radius": 5 * mm});
            skCircle(sketch, "E201.0", {"center": v(-83.32, 54.23) * mm, "radius": 45 * mm});
            skArc(sketch, "E202.1", {"start": v(-83.32, 99.23) * mm, "mid": v(-100.99, 97) * mm, "end": v(-117.55, 90.43) * mm});
            skCircle(sketch, "E203.0", {"center": v(-115.14, 86.05) * mm, "radius": 5 * mm});
            skArc(sketch, "E204.0", {"start": v(-119.52, 88.47) * mm, "mid": v(-126.08, 71.9) * mm, "end": v(-128.32, 54.23) * mm});
            skCircle(sketch, "E205.0", {"center": v(-115.14, -71.59) * mm, "radius": 5 * mm});
            skCircle(sketch, "E205.1", {"center": v(-115.14, -71.59) * mm, "radius": 1.65 * mm});
            skArc(sketch, "E206.0", {"start": v(10.68, -84.77) * mm, "mid": v(28.36, -82.53) * mm, "end": v(44.92, -75.97) * mm});
            skArc(sketch, "E206.1", {"start": v(46.88, -74) * mm, "mid": v(53.45, -57.44) * mm, "end": v(55.68, -39.77) * mm});
            skCircle(sketch, "E206.2", {"center": v(42.5, -71.59) * mm, "radius": 5 * mm});
            skCircle(sketch, "E206.3", {"center": v(42.5, -71.59) * mm, "radius": 1.65 * mm});
            skArc(sketch, "E207.0", {"start": v(-83.32, -84.77) * mm, "mid": v(-100.99, -82.53) * mm, "end": v(-117.55, -75.97) * mm});
            skArc(sketch, "E207.1", {"start": v(-119.52, -74) * mm, "mid": v(-126.08, -57.44) * mm, "end": v(-128.32, -39.77) * mm});
            skLineSegment(sketch, "E208.0", {"start": v(-48.32, 15.23) * mm, "end": v(-48.32, -0.77) * mm});
            skLineSegment(sketch, "E209.0", {"start": v(-24.32, 15.23) * mm, "end": v(-24.32, -0.77) * mm});
            skLineSegment(sketch, "E209.1", {"start": v(-21.32, 15.23) * mm, "end": v(-21.32, -0.77) * mm});
            skCircle(sketch, "E210.1", {"center": v(-115.14, 86.05) * mm, "radius": 1.65 * mm});
            skCircle(sketch, "E211.2", {"center": v(42.5, 86.05) * mm, "radius": 1.65 * mm});
            skSolve(sketch);
        }
        {
            var Q0;
            Q0=makeQuery(id+"F6.imprint","IMPRINT",FACE,{"disambiguationData":[TD([[makeQuery(id+"F6.imprint","IMPRINT",EDGE,{"derivedFrom":sQuery(id+"F6.wireOp",EDGE,"E67.0")}),1.0]])]});
            var Q1;
            {var subQ13=sQuery(id+"F6.wireOp",EDGE,"E97.0");Q1=makeQuery(id+"F6.imprint","IMPRINT",FACE,{"disambiguationData":[TD([[makeQuery(id+"F6.imprint","IMPRINT",EDGE,{"derivedFrom":subQ13}),1.0]])]});}
            var Q2;
            {var subQ0=sQuery(id+"F6.wireOp",EDGE,"E202.1");Q2=makeQuery(id+"F6.imprint","IMPRINT",FACE,{"disambiguationData":[TD([[makeQuery(id+"F6.imprint","IMPRINT",EDGE,{"derivedFrom":subQ0}),1.0]])]});}
            var Q3;
            {var subQ0=sQuery(id+"F6.wireOp",EDGE,"E203.0");var subQ1=sQuery(id+"F6.wireOp",EDGE,"E201.0");var subQ2=makeQuery(id+"F6.imprint","INTERSECT",VERTEX,{"disambiguationData":[OD(0.0)],"derivedFrom":[subQ1,subQ0]});Q3=makeQuery(id+"F6.imprint","IMPRINT",FACE,{"disambiguationData":[TD([[makeQuery(id+"F6.imprint","IMPRINT",EDGE,{"disambiguationData":[TD([[subQ2,-1.0]])],"derivedFrom":subQ1}),-1.0]])]});}
            var Q4;
            {var subQ0=sQuery(id+"F6.wireOp",EDGE,"E204.0");Q4=makeQuery(id+"F6.imprint","IMPRINT",FACE,{"disambiguationData":[TD([[makeQuery(id+"F6.imprint","IMPRINT",EDGE,{"derivedFrom":subQ0}),1.0]])]});}
            var Q5;
            {var subQ0=sQuery(id+"F6.wireOp",EDGE,"E198.0");Q5=makeQuery(id+"F6.imprint","IMPRINT",FACE,{"disambiguationData":[TD([[makeQuery(id+"F6.imprint","IMPRINT",EDGE,{"derivedFrom":subQ0}),-1.0]])]});}
            var Q6;
            {var subQ0=sQuery(id+"F6.wireOp",EDGE,"E200.2");var subQ1=sQuery(id+"F6.wireOp",EDGE,"E70.0");var subQ2=makeQuery(id+"F6.imprint","INTERSECT",VERTEX,{"disambiguationData":[OD(0.0)],"derivedFrom":[subQ1,subQ0]});Q6=makeQuery(id+"F6.imprint","IMPRINT",FACE,{"disambiguationData":[TD([[makeQuery(id+"F6.imprint","IMPRINT",EDGE,{"disambiguationData":[TD([[subQ2,-1.0]])],"derivedFrom":subQ1}),1.0]])]});}
            var Q7;
            {var subQ0=sQuery(id+"F6.wireOp",EDGE,"E199.1");Q7=makeQuery(id+"F6.imprint","IMPRINT",FACE,{"disambiguationData":[TD([[makeQuery(id+"F6.imprint","IMPRINT",EDGE,{"derivedFrom":subQ0}),-1.0]])]});}
            var Q8;
            {var subQ0=sQuery(id+"F6.wireOp",EDGE,"E192.MirrorCS");Q8=makeQuery(id+"F6.imprint","IMPRINT",FACE,{"disambiguationData":[TD([[makeQuery(id+"F6.imprint","IMPRINT",EDGE,{"derivedFrom":subQ0}),1.0]])]});}
            var Q9;
            {var subQ5=sQuery(id+"F6.wireOp",EDGE,"E114.MirrorCS");Q9=makeQuery(id+"F6.imprint","IMPRINT",FACE,{"disambiguationData":[TD([[makeQuery(id+"F6.imprint","IMPRINT",EDGE,{"derivedFrom":subQ5}),-1.0]])]});}
            var Q10;
            {var subQ3=sQuery(id+"F6.wireOp",EDGE,"E134.MirrorCS");Q10=makeQuery(id+"F6.imprint","IMPRINT",FACE,{"disambiguationData":[TD([[makeQuery(id+"F6.imprint","IMPRINT",EDGE,{"derivedFrom":subQ3}),1.0]])]});}
            var Q11;
            {var subQ0=sQuery(id+"F6.wireOp",EDGE,"E190");Q11=makeQuery(id+"F6.imprint","IMPRINT",FACE,{"disambiguationData":[TD([[makeQuery(id+"F6.imprint","IMPRINT",EDGE,{"derivedFrom":subQ0}),1.0]])]});}
            var Q12;
            Q12=makeQuery(id+"F6.imprint","IMPRINT",FACE,{"disambiguationData":[TD([[makeQuery(id+"F6.imprint","IMPRINT",EDGE,{"derivedFrom":sQuery(id+"F6.wireOp",EDGE,"E106")}),-1.0]])]});
            var Q13;
            {var subQ0=sQuery(id+"F6.wireOp",EDGE,"E104");Q13=makeQuery(id+"F6.imprint","IMPRINT",FACE,{"disambiguationData":[TD([[makeQuery(id+"F6.imprint","IMPRINT",EDGE,{"derivedFrom":subQ0}),-1.0]])]});}
            var Q14;
            {var subQ0=sQuery(id+"F6.wireOp",EDGE,"E194.MirrorCS");Q14=makeQuery(id+"F6.imprint","IMPRINT",FACE,{"disambiguationData":[TD([[makeQuery(id+"F6.imprint","IMPRINT",EDGE,{"derivedFrom":subQ0}),-1.0]])]});}
            var Q15;
            {var subQ0=sQuery(id+"F6.wireOp",EDGE,"E182.MirrorCS");Q15=makeQuery(id+"F6.imprint","IMPRINT",FACE,{"disambiguationData":[TD([[makeQuery(id+"F6.imprint","IMPRINT",EDGE,{"derivedFrom":subQ0}),1.0]])]});}
            var Q16;
            Q16=makeQuery(id+"F6.imprint","IMPRINT",FACE,{"disambiguationData":[TD([[makeQuery(id+"F6.imprint","IMPRINT",EDGE,{"derivedFrom":sQuery(id+"F6.wireOp",EDGE,"E205.1")}),1.0]])]});
            var Q17;
            {var subQ9=sQuery(id+"F6.wireOp",EDGE,"E137.MirrorCS");Q17=makeQuery(id+"F6.imprint","IMPRINT",FACE,{"disambiguationData":[TD([[makeQuery(id+"F6.imprint","IMPRINT",EDGE,{"derivedFrom":subQ9}),-1.0]])]});}
            var Q18;
            {var subQ0=sQuery(id+"F6.wireOp",EDGE,"E180.MirrorCS");Q18=makeQuery(id+"F6.imprint","IMPRINT",FACE,{"disambiguationData":[TD([[makeQuery(id+"F6.imprint","IMPRINT",EDGE,{"derivedFrom":subQ0}),-1.0]])]});}
            var Q19;
            {var subQ10=sQuery(id+"F6.wireOp",EDGE,"E159.MirrorCS");Q19=makeQuery(id+"F6.imprint","IMPRINT",FACE,{"disambiguationData":[TD([[makeQuery(id+"F6.imprint","IMPRINT",EDGE,{"derivedFrom":subQ10}),1.0]])]});}
            var Q20;
            {var subQ0=sQuery(id+"F6.wireOp",EDGE,"E196.MirrorCS");Q20=makeQuery(id+"F6.imprint","IMPRINT",FACE,{"disambiguationData":[TD([[makeQuery(id+"F6.imprint","IMPRINT",EDGE,{"derivedFrom":subQ0}),-1.0]])]});}
            var Q21;
            Q21=makeQuery(id+"F6.imprint","IMPRINT",FACE,{"disambiguationData":[TD([[makeQuery(id+"F6.imprint","IMPRINT",EDGE,{"derivedFrom":sQuery(id+"F6.wireOp",EDGE,"E206.3")}),-1.0]])]});
            var Q22;
            {var subQ0=sQuery(id+"F6.wireOp",EDGE,"E200.2");var subQ1=sQuery(id+"F6.wireOp",EDGE,"E70.0");var subQ2=makeQuery(id+"F6.imprint","INTERSECT",VERTEX,{"disambiguationData":[OD(0.0)],"derivedFrom":[subQ1,subQ0]});Q22=makeQuery(id+"F6.imprint","IMPRINT",FACE,{"disambiguationData":[TD([[makeQuery(id+"F6.imprint","IMPRINT",EDGE,{"disambiguationData":[TD([[subQ2,-1.0]])],"derivedFrom":subQ1}),-1.0]])]});}
            var Q23;
            {var subQ0=sQuery(id+"F6.wireOp",EDGE,"E203.0");var subQ1=sQuery(id+"F6.wireOp",EDGE,"E201.0");var subQ2=makeQuery(id+"F6.imprint","INTERSECT",VERTEX,{"disambiguationData":[OD(0.0)],"derivedFrom":[subQ1,subQ0]});Q23=makeQuery(id+"F6.imprint","IMPRINT",FACE,{"disambiguationData":[TD([[makeQuery(id+"F6.imprint","IMPRINT",EDGE,{"disambiguationData":[TD([[subQ2,-1.0]])],"derivedFrom":subQ1}),1.0]])]});}
            var Q24;
            {var subQ7=sQuery(id+"F6.wireOp",EDGE,"E78.0");var subQ8=makeQuery(id+"F6.imprint","INTERSECT",VERTEX,{"derivedFrom":[subQ7,sQuery(id+"F6.wireOp",EDGE,"E105")]});Q24=makeQuery(id+"F6.imprint","IMPRINT",FACE,{"disambiguationData":[TD([[makeQuery(id+"F6.imprint","IMPRINT",EDGE,{"disambiguationData":[TD([[subQ8,-1.0]])],"derivedFrom":subQ7}),-1.0]])]});}
            extrude(context, id + "F7", {"entities" : qUnion([Q0, Q1, Q2, Q3, Q4, Q5, Q6, Q7, Q8, Q9, Q10, Q11, Q12, Q13, Q14, Q15, Q16, Q17, Q18, Q19, Q20, Q21, Q22, Q23, Q24]), "depth" : 4 * mm});
        }
        {
            var Q0;
            Q0=makeQuery(id+"F7.opExtrude","SWEPT_EDGE",EDGE,{"disambiguationData":[OSD([sQuery(id+"F6.wireOp",EDGE,"E178.MirrorC"),sQuery(id+"F6.wireOp",EDGE,"E180.MirrorCS")])]});
            var Q1;
            Q1=makeQuery(id+"F7.opExtrude","SWEPT_EDGE",EDGE,{"disambiguationData":[OSD([sQuery(id+"F6.wireOp",EDGE,"E178.MirrorC"),sQuery(id+"F6.wireOp",EDGE,"E181.MirrorCS")])]});
            var Q2;
            Q2=makeQuery(id+"F7.opExtrude","SWEPT_EDGE",EDGE,{"disambiguationData":[OSD([sQuery(id+"F6.wireOp",EDGE,"E156.MirrorC"),sQuery(id+"F6.wireOp",EDGE,"E183.MirrorCS")])]});
            var Q3;
            Q3=makeQuery(id+"F7.opExtrude","SWEPT_EDGE",EDGE,{"disambiguationData":[OSD([sQuery(id+"F6.wireOp",EDGE,"E156.MirrorC"),sQuery(id+"F6.wireOp",EDGE,"E182.MirrorCS")])]});
            var Q4;
            Q4=makeQuery(id+"F7.opExtrude","SWEPT_EDGE",EDGE,{"disambiguationData":[OSD([sQuery(id+"F6.wireOp",EDGE,"E100"),sQuery(id+"F6.wireOp",EDGE,"E104")])]});
            var Q5;
            Q5=makeQuery(id+"F7.opExtrude","SWEPT_EDGE",EDGE,{"disambiguationData":[OSD([sQuery(id+"F6.wireOp",EDGE,"E100"),sQuery(id+"F6.wireOp",EDGE,"E105")])]});
            var Q6;
            Q6=makeQuery(id+"F7.opExtrude","SWEPT_EDGE",EDGE,{"disambiguationData":[OSD([sQuery(id+"F6.wireOp",EDGE,"E135.MirrorCS"),sQuery(id+"F6.wireOp",EDGE,"E136.MirrorC")])]});
            var Q7;
            Q7=makeQuery(id+"F7.opExtrude","SWEPT_EDGE",EDGE,{"disambiguationData":[OSD([sQuery(id+"F6.wireOp",EDGE,"E134.MirrorCS"),sQuery(id+"F6.wireOp",EDGE,"E136.MirrorC")])]});
            fillet(context, id + "F8", {"entities" : qUnion([Q0, Q1, Q2, Q3, Q4, Q5, Q6, Q7]), "radius" : 10 * mm, "tangentPropagation" : true, "allowEdgeOverflow" : false});
        }
        {
            var Q0;
            Q0=makeQuery(id+"F7.opExtrude","SWEPT_EDGE",EDGE,{"disambiguationData":[OSD([sQuery(id+"F6.wireOp",EDGE,"E78.0"),sQuery(id+"F6.wireOp",EDGE,"E105")])]});
            var Q1;
            Q1=makeQuery(id+"F7.opExtrude","SWEPT_EDGE",EDGE,{"disambiguationData":[OSD([sQuery(id+"F6.wireOp",EDGE,"E78.0"),sQuery(id+"F6.wireOp",EDGE,"E104")])]});
            var Q2;
            Q2=makeQuery(id+"F7.opExtrude","SWEPT_EDGE",EDGE,{"disambiguationData":[OSD([sQuery(id+"F6.wireOp",EDGE,"E79.0"),sQuery(id+"F6.wireOp",EDGE,"E134.MirrorCS")])]});
            var Q3;
            Q3=makeQuery(id+"F7.opExtrude","SWEPT_EDGE",EDGE,{"disambiguationData":[OSD([sQuery(id+"F6.wireOp",EDGE,"E76.0"),sQuery(id+"F6.wireOp",EDGE,"E181.MirrorCS")])]});
            var Q4;
            Q4=makeQuery(id+"F7.opExtrude","SWEPT_EDGE",EDGE,{"disambiguationData":[OSD([sQuery(id+"F6.wireOp",EDGE,"E76.0"),sQuery(id+"F6.wireOp",EDGE,"E180.MirrorCS")])]});
            var Q5;
            Q5=makeQuery(id+"F7.opExtrude","SWEPT_EDGE",EDGE,{"disambiguationData":[OSD([sQuery(id+"F6.wireOp",EDGE,"E79.0"),sQuery(id+"F6.wireOp",EDGE,"E135.MirrorCS")])]});
            var Q6;
            Q6=makeQuery(id+"F7.opExtrude","SWEPT_EDGE",EDGE,{"disambiguationData":[OSD([sQuery(id+"F6.wireOp",EDGE,"E77.0"),sQuery(id+"F6.wireOp",EDGE,"E182.MirrorCS")])]});
            var Q7;
            Q7=makeQuery(id+"F7.opExtrude","SWEPT_EDGE",EDGE,{"disambiguationData":[OSD([sQuery(id+"F6.wireOp",EDGE,"E77.0"),sQuery(id+"F6.wireOp",EDGE,"E183.MirrorCS")])]});
            fillet(context, id + "F9", {"entities" : qUnion([Q0, Q1, Q2, Q3, Q4, Q5, Q6, Q7]), "radius" : 5 * mm, "tangentPropagation" : true, "allowEdgeOverflow" : false});
        }
        {
            var Q0;
            Q0=makeQuery(id+"F7.opExtrude","SWEPT_EDGE",EDGE,{"disambiguationData":[OSD([sQuery(id+"F6.wireOp",EDGE,"E76.0"),sQuery(id+"F6.wireOp",EDGE,"f704e73e-0ce1-43f8-a8d8-0e1cfe47ec330.MirrorCS")])]});
            var Q1;
            Q1=makeQuery(id+"F7.opExtrude","SWEPT_EDGE",EDGE,{"disambiguationData":[OSD([sQuery(id+"F6.wireOp",EDGE,"E76.0"),sQuery(id+"F6.wireOp",EDGE,"a5165238-f0ac-4a22-a61f-a918f77715400.MirrorCS")])]});
            var Q2;
            Q2=makeQuery(id+"F7.opExtrude","SWEPT_EDGE",EDGE,{"disambiguationData":[OSD([sQuery(id+"F6.wireOp",EDGE,"E79.0"),sQuery(id+"F6.wireOp",EDGE,"2358d764-dcb7-4a1c-96ab-31910ee9d6890.MirrorCS")])]});
            var Q3;
            Q3=makeQuery(id+"F7.opExtrude","SWEPT_EDGE",EDGE,{"disambiguationData":[OSD([sQuery(id+"F6.wireOp",EDGE,"E79.0"),sQuery(id+"F6.wireOp",EDGE,"69ac0a36-7de7-4658-a2ba-9b21fc3682510.MirrorCS")])]});
            var Q4;
            Q4=makeQuery(id+"F7.opExtrude","SWEPT_EDGE",EDGE,{"disambiguationData":[OSD([sQuery(id+"F6.wireOp",EDGE,"E78.0"),sQuery(id+"F6.wireOp",EDGE,"yUtjuffF-P2Ux-gkCa-HPOt-JxYRPmwAUz8a")])]});
            var Q5;
            Q5=makeQuery(id+"F7.opExtrude","SWEPT_EDGE",EDGE,{"disambiguationData":[OSD([sQuery(id+"F6.wireOp",EDGE,"E78.0"),sQuery(id+"F6.wireOp",EDGE,"5ffJGHpK-FGRJ-3uTv-tFkD-v4DgQCtsBmpL")])]});
            var Q6;
            Q6=makeQuery(id+"F7.opExtrude","SWEPT_EDGE",EDGE,{"disambiguationData":[OSD([sQuery(id+"F6.wireOp",EDGE,"E77.0"),sQuery(id+"F6.wireOp",EDGE,"d686f993-c605-4d3e-b981-0ad73503aa210.MirrorCS")])]});
            var Q7;
            Q7=makeQuery(id+"F7.opExtrude","SWEPT_EDGE",EDGE,{"disambiguationData":[OSD([sQuery(id+"F6.wireOp",EDGE,"E77.0"),sQuery(id+"F6.wireOp",EDGE,"69663404-4aa5-4212-a2cc-a3d8aa77b83a0.MirrorCS")])]});
            fillet(context, id + "F10", {"entities" : qUnion([Q0, Q1, Q2, Q3, Q4, Q5, Q6, Q7]), "radius" : 5 * mm, "tangentPropagation" : true, "allowEdgeOverflow" : false});
        }
        {
            var Q0;
            Q0=makeQuery(id+"F7.opExtrude","SWEPT_EDGE",EDGE,{"disambiguationData":[OSD([sQuery(id+"F6.wireOp",EDGE,"E69.0"),sQuery(id+"F6.wireOp",EDGE,"E188.MirrorCS")])]});
            var Q1;
            Q1=makeQuery(id+"F7.opExtrude","SWEPT_EDGE",EDGE,{"disambiguationData":[OSD([sQuery(id+"F6.wireOp",EDGE,"E69.0"),sQuery(id+"F6.wireOp",EDGE,"E185")])]});
            fillet(context, id + "F11", {"entities" : qUnion([Q0, Q1]), "radius" : 5 * mm, "tangentPropagation" : true, "allowEdgeOverflow" : false});
        }
        {
            var Q0;
            Q0=makeQuery(id+"F7.opExtrude","SWEPT_EDGE",EDGE,{"disambiguationData":[OSD([sQuery(id+"F6.wireOp",EDGE,"E187.MirrorCS"),sQuery(id+"F6.wireOp",EDGE,"E188.MirrorCS")])]});
            var Q1;
            Q1=makeQuery(id+"F7.opExtrude","SWEPT_EDGE",EDGE,{"disambiguationData":[OSD([sQuery(id+"F6.wireOp",EDGE,"E185"),sQuery(id+"F6.wireOp",EDGE,"E186")])]});
            fillet(context, id + "F12", {"entities" : qUnion([Q0, Q1]), "radius" : 5 * mm, "tangentPropagation" : true, "allowEdgeOverflow" : false});
        }
        {
            var Q0;
            Q0=makeQuery(id+"F7.opExtrude","SWEPT_EDGE",EDGE,{"disambiguationData":[OSD([sQuery(id+"F6.wireOp",EDGE,"E100"),sQuery(id+"F6.wireOp",EDGE,"E190")])]});
            var Q1;
            Q1=makeQuery(id+"F7.opExtrude","SWEPT_EDGE",EDGE,{"disambiguationData":[OSD([sQuery(id+"F6.wireOp",EDGE,"E136.MirrorC"),sQuery(id+"F6.wireOp",EDGE,"E193.MirrorCS")])]});
            var Q2;
            Q2=makeQuery(id+"F7.opExtrude","SWEPT_EDGE",EDGE,{"disambiguationData":[OSD([sQuery(id+"F6.wireOp",EDGE,"E156.MirrorC"),sQuery(id+"F6.wireOp",EDGE,"E195.MirrorCS")])]});
            var Q3;
            Q3=makeQuery(id+"F7.opExtrude","SWEPT_EDGE",EDGE,{"disambiguationData":[OSD([sQuery(id+"F6.wireOp",EDGE,"E100"),sQuery(id+"F6.wireOp",EDGE,"E191")])]});
            var Q4;
            Q4=makeQuery(id+"F7.opExtrude","SWEPT_EDGE",EDGE,{"disambiguationData":[OSD([sQuery(id+"F6.wireOp",EDGE,"E136.MirrorC"),sQuery(id+"F6.wireOp",EDGE,"E192.MirrorCS")])]});
            var Q5;
            Q5=makeQuery(id+"F7.opExtrude","SWEPT_EDGE",EDGE,{"disambiguationData":[OSD([sQuery(id+"F6.wireOp",EDGE,"E178.MirrorC"),sQuery(id+"F6.wireOp",EDGE,"E197.MirrorCS")])]});
            var Q6;
            Q6=makeQuery(id+"F7.opExtrude","SWEPT_EDGE",EDGE,{"disambiguationData":[OSD([sQuery(id+"F6.wireOp",EDGE,"E178.MirrorC"),sQuery(id+"F6.wireOp",EDGE,"E196.MirrorCS")])]});
            var Q7;
            Q7=makeQuery(id+"F7.opExtrude","SWEPT_EDGE",EDGE,{"disambiguationData":[OSD([sQuery(id+"F6.wireOp",EDGE,"E156.MirrorC"),sQuery(id+"F6.wireOp",EDGE,"E194.MirrorCS")])]});
            fillet(context, id + "F13", {"entities" : qUnion([Q0, Q1, Q2, Q3, Q4, Q5, Q6, Q7]), "radius" : 5 * mm, "tangentPropagation" : true, "allowEdgeOverflow" : false});
        }
    });
